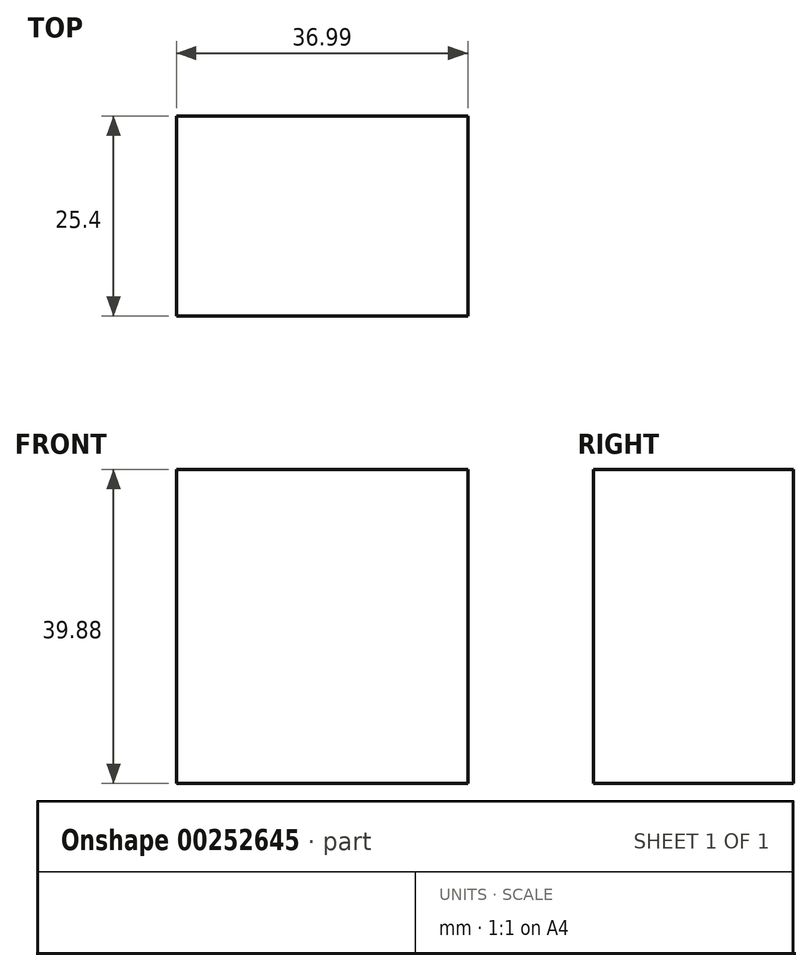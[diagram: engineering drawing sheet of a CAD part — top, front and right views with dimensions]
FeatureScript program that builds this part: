
annotation { "Feature Type Name" : "Feature", "Feature Type Description" : "" }
export const myFeature = defineFeature(function(context is Context, id is Id, definition is map)
    precondition{}
    {
        {
            var Q0;
            Q0=qCreatedBy(makeId("Front.planeOp"),FACE);
            var sketch = newSketch(context, id + "F0", { "sketchPlane" : qUnion([Q0])});
            skLineSegment(sketch, "E0.bottom", {"start": v(0, 0) * mm, "end": v(37, 0) * mm});
            skLineSegment(sketch, "E0.top", {"start": v(0, 39.88) * mm, "end": v(37, 39.88) * mm});
            skLineSegment(sketch, "E0.left", {"start": v(0, 0) * mm, "end": v(0, 39.88) * mm});
            skLineSegment(sketch, "E0.right", {"start": v(37, 0) * mm, "end": v(37, 39.88) * mm});
            skSolve(sketch);
        }
        {
            var Q0;
            Q0=makeQuery(id+"F0.imprint","IMPRINT",FACE,{"disambiguationData":[TD([[makeQuery(id+"F0.imprint","IMPRINT",EDGE,{"derivedFrom":sQuery(id+"F0.wireOp",EDGE,"E0.bottom")}),1.0]])]});
            extrude(context, id + "F1", {"entities" : qUnion([Q0]), "depth" : 25.4 * mm});
        }
    });
